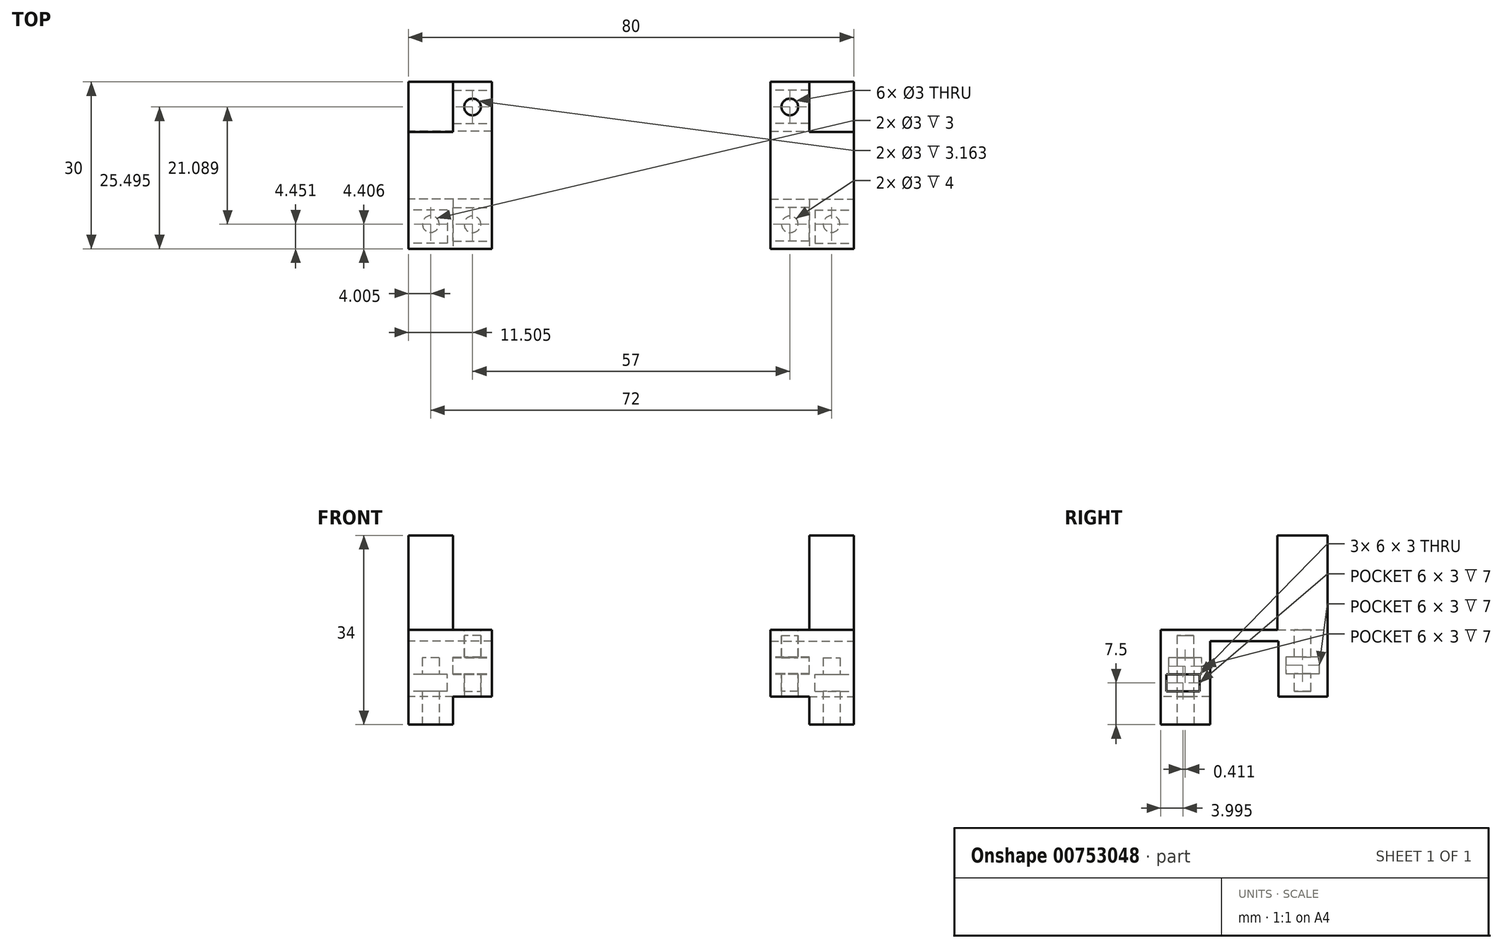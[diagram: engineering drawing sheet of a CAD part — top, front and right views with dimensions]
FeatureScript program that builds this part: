
annotation { "Feature Type Name" : "Feature", "Feature Type Description" : "" }
export const myFeature = defineFeature(function(context is Context, id is Id, definition is map)
    precondition{}
    {
        {
            var Q0;
            Q0=qCreatedBy(makeId("Top.planeOp"),FACE);
            var sketch = newSketch(context, id + "F0", { "sketchPlane" : qUnion([Q0])});
            skLineSegment(sketch, "E0.bottom", {"start": v(-0.18, 16.84) * mm, "end": v(14.82, 16.84) * mm});
            skLineSegment(sketch, "E0.top", {"start": v(-0.18, -13.16) * mm, "end": v(14.82, -13.16) * mm});
            skLineSegment(sketch, "E0.left", {"start": v(-0.18, 16.84) * mm, "end": v(-0.18, -13.16) * mm});
            skLineSegment(sketch, "E0.right", {"start": v(14.82, 16.84) * mm, "end": v(14.82, -13.16) * mm});
            skLineSegment(sketch, "E1", {"start": v(14.82, 7.84) * mm, "end": v(6.82, 7.84) * mm});
            skLineSegment(sketch, "E2", {"start": v(6.82, 7.84) * mm, "end": v(6.82, 16.84) * mm});
            skPoint(sketch, "E2.endSnap0", {"position": v(7.32, 16.84) * mm});
            skLineSegment(sketch, "E3", {"start": v(14.82, -13.16) * mm, "end": v(13.82, -13.16) * mm});
            skLineSegment(sketch, "E4", {"start": v(13.82, -13.16) * mm, "end": v(13.82, 7.84) * mm});
            skSolve(sketch);
        }
        {
            var Q0;
            {var subQ4=sQuery(id+"F0.wireOp",EDGE,"E2");Q0=makeQuery(id+"F0.imprint","IMPRINT",FACE,{"disambiguationData":[TD([[makeQuery(id+"F0.imprint","IMPRINT",EDGE,{"derivedFrom":subQ4}),-1.0]])]});}
            extrude(context, id + "F1", {"entities" : qUnion([Q0]), "depth" : 29 * mm, "offsetDistance" : 25 * mm});
        }
        {
            var Q0;
            {var subQ3=sQuery(id+"F0.wireOp",EDGE,"E4");Q0=makeQuery(id+"F0.imprint","IMPRINT",FACE,{"disambiguationData":[TD([[makeQuery(id+"F0.imprint","IMPRINT",EDGE,{"derivedFrom":subQ3}),-1.0]])]});}
            extrude(context, id + "F2", {"entities" : qUnion([Q0]), "operationType" : NewBodyOperationType.ADD, "depth" : 29 * mm, "offsetDistance" : 25 * mm});
        }
        {
            var Q0;
            {var subQ0=sQuery(id+"F0.wireOp",EDGE,"E0.left");Q0=makeQuery(id+"F0.imprint","IMPRINT",FACE,{"disambiguationData":[TD([[makeQuery(id+"F0.imprint","IMPRINT",EDGE,{"derivedFrom":subQ0}),1.0]])]});}
            extrude(context, id + "F3", {"entities" : qUnion([Q0]), "operationType" : NewBodyOperationType.ADD, "depth" : 12 * mm, "offsetDistance" : 25 * mm});
        }
        {
            var Q0;
            Q0=qCreatedBy(makeId("Right.planeOp"),FACE);
            var sketch = newSketch(context, id + "F4", { "sketchPlane" : qUnion([Q0])});
            skLineSegment(sketch, "E5", {"start": v(7.97, 0) * mm, "end": v(7.97, 10) * mm});
            skLineSegment(sketch, "E6", {"start": v(-4.25, 0) * mm, "end": v(-4.25, 10) * mm});
            skLineSegment(sketch, "E7", {"start": v(-4.25, 10) * mm, "end": v(7.97, 10) * mm});
            skLineSegment(sketch, "E8", {"start": v(7.97, 0) * mm, "end": v(-4.25, 0) * mm});
            skSolve(sketch);
        }
        {
            var Q0;
            Q0=qSketchRegion(id+"F4",true);
            extrude(context, id + "F5", {"entities" : qUnion([Q0]), "operationType" : NewBodyOperationType.ADD, "depth" : 15 * mm, "offsetDistance" : 25 * mm});
        }
        {
            var Q0;
            Q0=makeQuery(id+"F5.opExtrude","CAP_FACE",FACE,{"disambiguationData":[OSD([sQuery(id+"F4.wireOp",EDGE,"E5"),sQuery(id+"F4.wireOp",EDGE,"E6"),sQuery(id+"F4.wireOp",EDGE,"E7"),sQuery(id+"F4.wireOp",EDGE,"E8")])],"isStart":false});
            extrude(context, id + "F6", {"entities" : qUnion([Q0]), "operationType" : NewBodyOperationType.REMOVE, "oppositeDirection" : true, "depth" : 16 * mm, "offsetDistance" : 25 * mm});
        }
        {
            var Q0;
            {var subQ0=sQuery(id+"F0.wireOp",EDGE,"E0.right");var subQ1=sQuery(id+"F0.wireOp",EDGE,"E0.top");var subQ2=sQuery(id+"F0.wireOp",EDGE,"E0.left");var subQ3=sQuery(id+"F0.wireOp",EDGE,"E4");var subQ4=sQuery(id+"F0.wireOp",EDGE,"E2");var subQ5=sQuery(id+"F0.wireOp",EDGE,"E1");var subQ6=sQuery(id+"F0.wireOp",EDGE,"E0.bottom");Q0=makeQuery(id+"F6.boolean.opBoolean","SPLIT",FACE,{"disambiguationData":[TD([makeQuery(id+"F2.opExtrude","SWEPT_FACE",FACE,{"disambiguationData":[OSD([subQ1])]})])],"derivedFrom":makeQuery(id+"F5.boolean.opBoolean","MERGE",FACE,{"derivedFrom":[makeQuery(id+"F3.boolean.opBoolean","MERGE",FACE,{"derivedFrom":[makeQuery(id+"F2.boolean.opBoolean","MERGE",FACE,{"derivedFrom":[makeQuery(id+"F1.opExtrude","CAP_FACE",FACE,{"disambiguationData":[OSD([subQ6,subQ0,subQ5,subQ4])],"isStart":true}),makeQuery(id+"F2.opExtrude","CAP_FACE",FACE,{"disambiguationData":[OSD([subQ1,subQ0,subQ5,subQ3])],"isStart":true})]}),makeQuery(id+"F3.opExtrude","CAP_FACE",FACE,{"disambiguationData":[OSD([subQ6,subQ1,subQ2,subQ5,subQ4,subQ3])],"isStart":true})]}),makeQuery(id+"F5.opExtrude","SWEPT_FACE",FACE,{"disambiguationData":[OSD([sQuery(id+"F4.wireOp",EDGE,"E8")])]})]})});}
            var sketch = newSketch(context, id + "F7", { "sketchPlane" : qUnion([Q0])});
            skLineSegment(sketch, "E9", {"start": v(14.82, 4.25) * mm, "end": v(6.82, 4.25) * mm});
            skLineSegment(sketch, "E10", {"start": v(6.82, 4.25) * mm, "end": v(6.82, 13.16) * mm});
            skLineSegment(sketch, "E11", {"start": v(6.82, 13.16) * mm, "end": v(14.82, 13.16) * mm});
            skLineSegment(sketch, "E12", {"start": v(14.82, 13.16) * mm, "end": v(14.82, 4.25) * mm});
            skSolve(sketch);
        }
        {
            var Q0;
            Q0=makeQuery(id+"F7.imprint","IMPRINT",FACE,{"disambiguationData":[TD([[makeQuery(id+"F7.imprint","IMPRINT",EDGE,{"derivedFrom":sQuery(id+"F7.wireOp",EDGE,"E9")}),1.0]])]});
            extrude(context, id + "F8", {"entities" : qUnion([Q0]), "operationType" : NewBodyOperationType.ADD, "depth" : 5 * mm, "offsetDistance" : 25 * mm});
        }
        {
            var Q0;
            Q0=makeQuery(id+"F8.opExtrude","CAP_FACE",FACE,{"disambiguationData":[OSD([sQuery(id+"F7.wireOp",EDGE,"E9"),sQuery(id+"F7.wireOp",EDGE,"E10"),sQuery(id+"F7.wireOp",EDGE,"E11"),sQuery(id+"F7.wireOp",EDGE,"E12")])],"isStart":false});
            var sketch = newSketch(context, id + "F9", { "sketchPlane" : qUnion([Q0])});
            skLineSegment(sketch, "E13", {"start": v(6.82, 13.16) * mm, "end": v(10.82, 13.16) * mm});
            skLineSegment(sketch, "E14", {"start": v(10.82, 13.16) * mm, "end": v(10.82, 4.25) * mm});
            skLineSegment(sketch, "E15", {"start": v(10.82, 4.25) * mm, "end": v(10.82, 8.7) * mm});
            skLineSegment(sketch, "E16", {"start": v(10.82, 8.7) * mm, "end": v(14.82, 8.7) * mm});
            skLineSegment(sketch, "E17", {"start": v(14.82, 8.7) * mm, "end": v(6.82, 8.7) * mm});
            skCircle(sketch, "E18", {"center": v(10.82, 8.7) * mm, "radius": 1.5 * mm});
            skSolve(sketch);
        }
        {
            var Q0;
            {var subQ1=sQuery(id+"F9.wireOp",EDGE,"E14");var subQ3=sQuery(id+"F9.wireOp",EDGE,"E18");var subQ4=makeQuery(id+"F9.imprint","INTERSECT",VERTEX,{"derivedFrom":[subQ1,subQ3]});Q0=makeQuery(id+"F9.imprint","IMPRINT",FACE,{"disambiguationData":[TD([[makeQuery(id+"F9.imprint","IMPRINT",EDGE,{"disambiguationData":[TD([[subQ4,1.0]])],"derivedFrom":subQ3}),1.0]])]});}
            var Q1;
            {var subQ1=sQuery(id+"F9.wireOp",EDGE,"E15");var subQ3=sQuery(id+"F9.wireOp",EDGE,"E18");var subQ4=makeQuery(id+"F9.imprint","INTERSECT",VERTEX,{"derivedFrom":[subQ1,subQ3]});Q1=makeQuery(id+"F9.imprint","IMPRINT",FACE,{"disambiguationData":[TD([[makeQuery(id+"F9.imprint","IMPRINT",EDGE,{"disambiguationData":[TD([[subQ4,-1.0]])],"derivedFrom":subQ3}),1.0]])]});}
            var Q2;
            {var subQ1=sQuery(id+"F9.wireOp",EDGE,"E15");var subQ3=sQuery(id+"F9.wireOp",EDGE,"E18");var subQ4=makeQuery(id+"F9.imprint","INTERSECT",VERTEX,{"derivedFrom":[subQ1,subQ3]});Q2=makeQuery(id+"F9.imprint","IMPRINT",FACE,{"disambiguationData":[TD([[makeQuery(id+"F9.imprint","IMPRINT",EDGE,{"disambiguationData":[TD([[subQ4,1.0]])],"derivedFrom":subQ3}),1.0]])]});}
            var Q3;
            {var subQ1=sQuery(id+"F9.wireOp",EDGE,"E14");var subQ3=sQuery(id+"F9.wireOp",EDGE,"E18");var subQ4=makeQuery(id+"F9.imprint","INTERSECT",VERTEX,{"derivedFrom":[subQ1,subQ3]});Q3=makeQuery(id+"F9.imprint","IMPRINT",FACE,{"disambiguationData":[TD([[makeQuery(id+"F9.imprint","IMPRINT",EDGE,{"disambiguationData":[TD([[subQ4,-1.0]])],"derivedFrom":subQ3}),1.0]])]});}
            extrude(context, id + "F10", {"entities" : qUnion([Q0, Q1, Q2, Q3]), "operationType" : NewBodyOperationType.REMOVE, "oppositeDirection" : true, "depth" : 12 * mm, "offsetDistance" : 25 * mm});
        }
        {
            var Q0;
            {var subQ0=sQuery(id+"F0.wireOp",EDGE,"E0.right");Q0=makeQuery(id+"F8.boolean.opBoolean","MERGE",FACE,{"derivedFrom":[makeQuery(id+"F2.boolean.opBoolean","MERGE",FACE,{"derivedFrom":[makeQuery(id+"F1.opExtrude","SWEPT_FACE",FACE,{"disambiguationData":[OSD([subQ0])]}),makeQuery(id+"F2.opExtrude","SWEPT_FACE",FACE,{"disambiguationData":[OSD([subQ0])]})]}),makeQuery(id+"F8.opExtrude","SWEPT_FACE",FACE,{"disambiguationData":[OSD([sQuery(id+"F7.wireOp",EDGE,"E12")])]})]});}
            var sketch = newSketch(context, id + "F11", { "sketchPlane" : qUnion([Q0])});
            skLineSegment(sketch, "E19", {"start": v(-12.16, 1) * mm, "end": v(-12.16, 4) * mm});
            skLineSegment(sketch, "E20", {"start": v(-12.16, 4) * mm, "end": v(-6.16, 4) * mm});
            skLineSegment(sketch, "E21", {"start": v(-6.16, 4) * mm, "end": v(-6.16, 1) * mm});
            skLineSegment(sketch, "E22", {"start": v(-6.16, 1) * mm, "end": v(-12.16, 1) * mm});
            skSolve(sketch);
        }
        {
            var Q0;
            Q0=makeQuery(id+"F11.imprint","IMPRINT",FACE,{"disambiguationData":[TD([[makeQuery(id+"F11.imprint","IMPRINT",EDGE,{"derivedFrom":sQuery(id+"F11.wireOp",EDGE,"E19")}),-1.0]])]});
            extrude(context, id + "F12", {"entities" : qUnion([Q0]), "operationType" : NewBodyOperationType.REMOVE, "oppositeDirection" : true, "depth" : 7 * mm, "offsetDistance" : 25 * mm});
        }
        {
            var Q0;
            Q0=makeQuery(id+"F3.opExtrude","SWEPT_FACE",FACE,{"disambiguationData":[OSD([sQuery(id+"F0.wireOp",EDGE,"E0.left")])]});
            var sketch = newSketch(context, id + "F13", { "sketchPlane" : qUnion([Q0])});
            skLineSegment(sketch, "E23", {"start": v(-15.34, 4.16) * mm, "end": v(-15.34, 7.16) * mm});
            skLineSegment(sketch, "E24", {"start": v(-15.34, 7.16) * mm, "end": v(-9.34, 7.16) * mm});
            skLineSegment(sketch, "E25", {"start": v(-9.34, 7.16) * mm, "end": v(-9.34, 4.16) * mm});
            skLineSegment(sketch, "E26", {"start": v(-9.34, 4.16) * mm, "end": v(-15.34, 4.16) * mm});
            skLineSegment(sketch, "E27", {"start": v(5.75, 4) * mm, "end": v(5.75, 7) * mm});
            skLineSegment(sketch, "E28", {"start": v(5.75, 7) * mm, "end": v(11.75, 7) * mm});
            skLineSegment(sketch, "E29", {"start": v(11.75, 7) * mm, "end": v(11.75, 4) * mm});
            skLineSegment(sketch, "E30", {"start": v(11.75, 4) * mm, "end": v(5.75, 4) * mm});
            skSolve(sketch);
        }
        {
            var Q0;
            Q0=makeQuery(id+"F13.imprint","IMPRINT",FACE,{"disambiguationData":[TD([[makeQuery(id+"F13.imprint","IMPRINT",EDGE,{"derivedFrom":sQuery(id+"F13.wireOp",EDGE,"E23")}),-1.0]])]});
            extrude(context, id + "F14", {"entities" : qUnion([Q0]), "operationType" : NewBodyOperationType.REMOVE, "oppositeDirection" : true, "depth" : 7 * mm, "offsetDistance" : 25 * mm});
        }
        {
            var Q0;
            Q0=makeQuery(id+"F3.opExtrude","CAP_FACE",FACE,{"disambiguationData":[OSD([sQuery(id+"F0.wireOp",EDGE,"E0.bottom"),sQuery(id+"F0.wireOp",EDGE,"E0.top"),sQuery(id+"F0.wireOp",EDGE,"E0.left"),sQuery(id+"F0.wireOp",EDGE,"E1"),sQuery(id+"F0.wireOp",EDGE,"E2"),sQuery(id+"F0.wireOp",EDGE,"E4")])],"isStart":false});
            var sketch = newSketch(context, id + "F15", { "sketchPlane" : qUnion([Q0])});
            skLineSegment(sketch, "E31", {"start": v(6.82, 16.84) * mm, "end": v(6.82, 12.34) * mm});
            skCircle(sketch, "E32", {"center": v(3.32, 12.34) * mm, "radius": 1.5 * mm});
            skSolve(sketch);
        }
        {
            var Q0;
            Q0=makeQuery(id+"F15.imprint","IMPRINT",FACE,{"disambiguationData":[TD([[makeQuery(id+"F15.imprint","IMPRINT",EDGE,{"derivedFrom":sQuery(id+"F15.wireOp",EDGE,"E32")}),1.0]])]});
            extrude(context, id + "F16", {"entities" : qUnion([Q0]), "operationType" : NewBodyOperationType.REMOVE, "oppositeDirection" : true, "depth" : 11 * mm, "offsetDistance" : 25 * mm});
        }
        {
            var Q0;
            Q0=qSketchRegion(id+"F13",true);
            extrude(context, id + "F17", {"entities" : qUnion([Q0]), "operationType" : NewBodyOperationType.REMOVE, "oppositeDirection" : true, "depth" : 7 * mm, "offsetDistance" : 25 * mm});
        }
        {
            var Q0;
            {var subQ0=sQuery(id+"F0.wireOp",EDGE,"E0.right");var subQ1=sQuery(id+"F0.wireOp",EDGE,"E0.top");var subQ2=sQuery(id+"F0.wireOp",EDGE,"E0.left");var subQ3=sQuery(id+"F0.wireOp",EDGE,"E4");var subQ4=sQuery(id+"F0.wireOp",EDGE,"E2");var subQ5=sQuery(id+"F0.wireOp",EDGE,"E1");var subQ6=sQuery(id+"F0.wireOp",EDGE,"E0.bottom");Q0=makeQuery(id+"F6.boolean.opBoolean","SPLIT",FACE,{"disambiguationData":[TD([makeQuery(id+"F2.opExtrude","SWEPT_FACE",FACE,{"disambiguationData":[OSD([subQ1])]})])],"derivedFrom":makeQuery(id+"F5.boolean.opBoolean","MERGE",FACE,{"derivedFrom":[makeQuery(id+"F3.boolean.opBoolean","MERGE",FACE,{"derivedFrom":[makeQuery(id+"F2.boolean.opBoolean","MERGE",FACE,{"derivedFrom":[makeQuery(id+"F1.opExtrude","CAP_FACE",FACE,{"disambiguationData":[OSD([subQ6,subQ0,subQ5,subQ4])],"isStart":true}),makeQuery(id+"F2.opExtrude","CAP_FACE",FACE,{"disambiguationData":[OSD([subQ1,subQ0,subQ5,subQ3])],"isStart":true})]}),makeQuery(id+"F3.opExtrude","CAP_FACE",FACE,{"disambiguationData":[OSD([subQ6,subQ1,subQ2,subQ5,subQ4,subQ3])],"isStart":true})]}),makeQuery(id+"F5.opExtrude","SWEPT_FACE",FACE,{"disambiguationData":[OSD([sQuery(id+"F4.wireOp",EDGE,"E8")])]})]})});}
            var sketch = newSketch(context, id + "F18", { "sketchPlane" : qUnion([Q0])});
            skCircle(sketch, "E33", {"center": v(3.32, 8.75) * mm, "radius": 1.5 * mm});
            skSolve(sketch);
        }
        {
            var Q0;
            Q0=makeQuery(id+"F18.imprint","IMPRINT",FACE,{"disambiguationData":[TD([[makeQuery(id+"F18.imprint","IMPRINT",EDGE,{"derivedFrom":sQuery(id+"F18.wireOp",EDGE,"E33")}),1.0]])]});
            extrude(context, id + "F19", {"entities" : qUnion([Q0]), "operationType" : NewBodyOperationType.REMOVE, "oppositeDirection" : true, "depth" : 11 * mm, "offsetDistance" : 25 * mm});
        }
        {
            var Q0;
            Q0=makeQuery(id+"F2.opExtrude","SWEPT_FACE",FACE,{"disambiguationData":[OSD([sQuery(id+"F0.wireOp",EDGE,"E4")])]});
            var sketch = newSketch(context, id + "F20", { "sketchPlane" : qUnion([Q0])});
            skSolve(sketch);
        }
        {
            var Q0;
            Q0=qSketchRegion(id+"F20",true);
            var Q1;
            {var subQ0=sQuery(id+"F0.wireOp",EDGE,"E4");Q1=makeQuery(id+"F20.imprint","IMPRINT",FACE,{"disambiguationData":[TD([[makeQuery(id+"F20.imprint","IMPRINT",EDGE,{"derivedFrom":makeQuery(id+"F2.opExtrude","CAP_EDGE",EDGE,{"disambiguationData":[OSD([subQ0])],"isStart":false})}),1.0]])]});}
            extrude(context, id + "F21", {"entities" : qUnion([Q0, Q1]), "operationType" : NewBodyOperationType.REMOVE, "oppositeDirection" : true, "depth" : 1 * mm, "offsetDistance" : 25 * mm});
        }
        {
            var Q0;
            Q0=makeQuery(id+"F3.opExtrude","SWEPT_FACE",FACE,{"disambiguationData":[OSD([sQuery(id+"F0.wireOp",EDGE,"E0.left")])]});
            cPlane(context, id + "F22", {"entities" : qUnion([Q0]), "cplaneType" : CPlaneType.OFFSET, "offset" : 25 * mm, "width" : 150 * mm, "height" : 150 * mm});
        }
        {
            var Q0;
            Q0=makeQuery(id+"F1.opExtrude","SWEPT_BODY",BODY,{"disambiguationData":[OSD([sQuery(id+"F0.wireOp",EDGE,"E0.bottom"),sQuery(id+"F0.wireOp",EDGE,"E0.right"),sQuery(id+"F0.wireOp",EDGE,"E1"),sQuery(id+"F0.wireOp",EDGE,"E2")])]});
            var Q1;
            Q1=qCreatedBy(id+"F22.planeOp",FACE);
            mirror(context, id + "F23", {"entities" : qUnion([Q0]), "mirrorPlane" : qUnion([Q1])});
        }
    });
